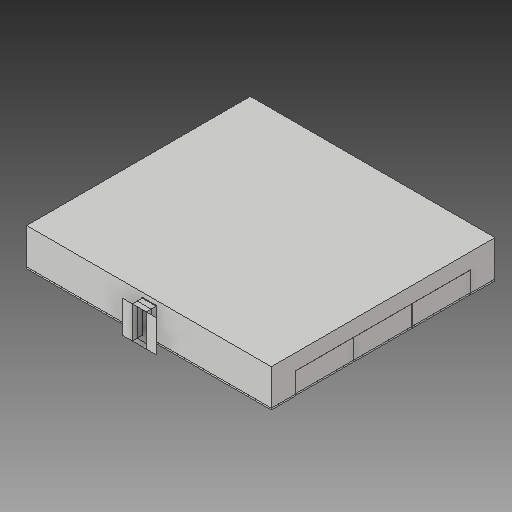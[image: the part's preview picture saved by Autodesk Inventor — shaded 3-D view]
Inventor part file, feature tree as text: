
AUTODESK INVENTOR PART (.ipt)
format: ipt  version: 2017 (Build 210142000, 142)  size: 561,664 bytes
history: native  units: in
note: dims shown in document units (in); Inventor stores cm internally (conversion verified against a paired STEP export)
features: extrude x9, sketch x7, delete_face x2
ambient origin geometry x8: Origin, YZ Plane, XZ Plane, XY Plane, X Axis, Y Axis, Z Axis, Center Point
bodies: Solid1 (feature_tree), Solid3 (feature_tree)
feature tree (18):
  extrude  "cubicals"  Depth=12.0in
  extrude  "floor"  Depth=2.5in
  extrude  "walls"  Depth=0.0833in
  extrude  "connection"  Depth=0.0833in
  extrude  "connection cut"  Depth=2.5in
  extrude  "ceiling"  Depth=0.0104in
  extrude  "door trim"  Depth=0.0104in
  extrude  "door trim top"  Depth=6.0in
  extrude  "floor trim"  Depth=6.0in
  delete_face  "Delete Face1"
  delete_face  "Delete Face2"
  sketch  "Sketch2"  dims[d2=4.5in d3=0.0in d4=12.0in]
  sketch  "Sketch3"  dims[d5=8.0in d7=2.5in]
  sketch  "Sketch6"  dims[d10=0.0833in d95=0.0833in]
  sketch  "Sketch7"  dims[d97=0.0833in d98=0.0833in]
  sketch  "Sketch8"  dims[d99=12.0in d100=8.0in d102=0.0833in d103=0.0833in d104=0.0833in d105=0.0833in]
  sketch  "Sketch9"  dims[d106=12.0in d107=8.0in d109=0.0833in d110=0.0833in d111=0.0833in d112=0.0833in d113=2.5in]
  sketch  "Sketch10"  dims[d114=2.5in d115=3.0in d117=3.0in d118=6.0in d120=6.0in d121=1.0in d122=0.0in d128=1.0in d129=1.0in d130=1.0in d131=1.0in d132=1.0in d133=1.0in d134=7.7746in d135=0.0in d160=1.0in d161=0.0in d171=1.0in d172=0.0in d173=1.0in d174=0.0in d191=1.4375in d192=6.6667in d193=2.875in d194=7.0in d195=6.6667in d200=0.0417in d201=0.1667in d202=1.0in d203=0.0in d204=0.1667in d205=1.0in d206=0.0in d207=0.0104in d208=0.3438in d209=0.0in d210=0.0104in d211=0.0104in d212=0.0104in]
